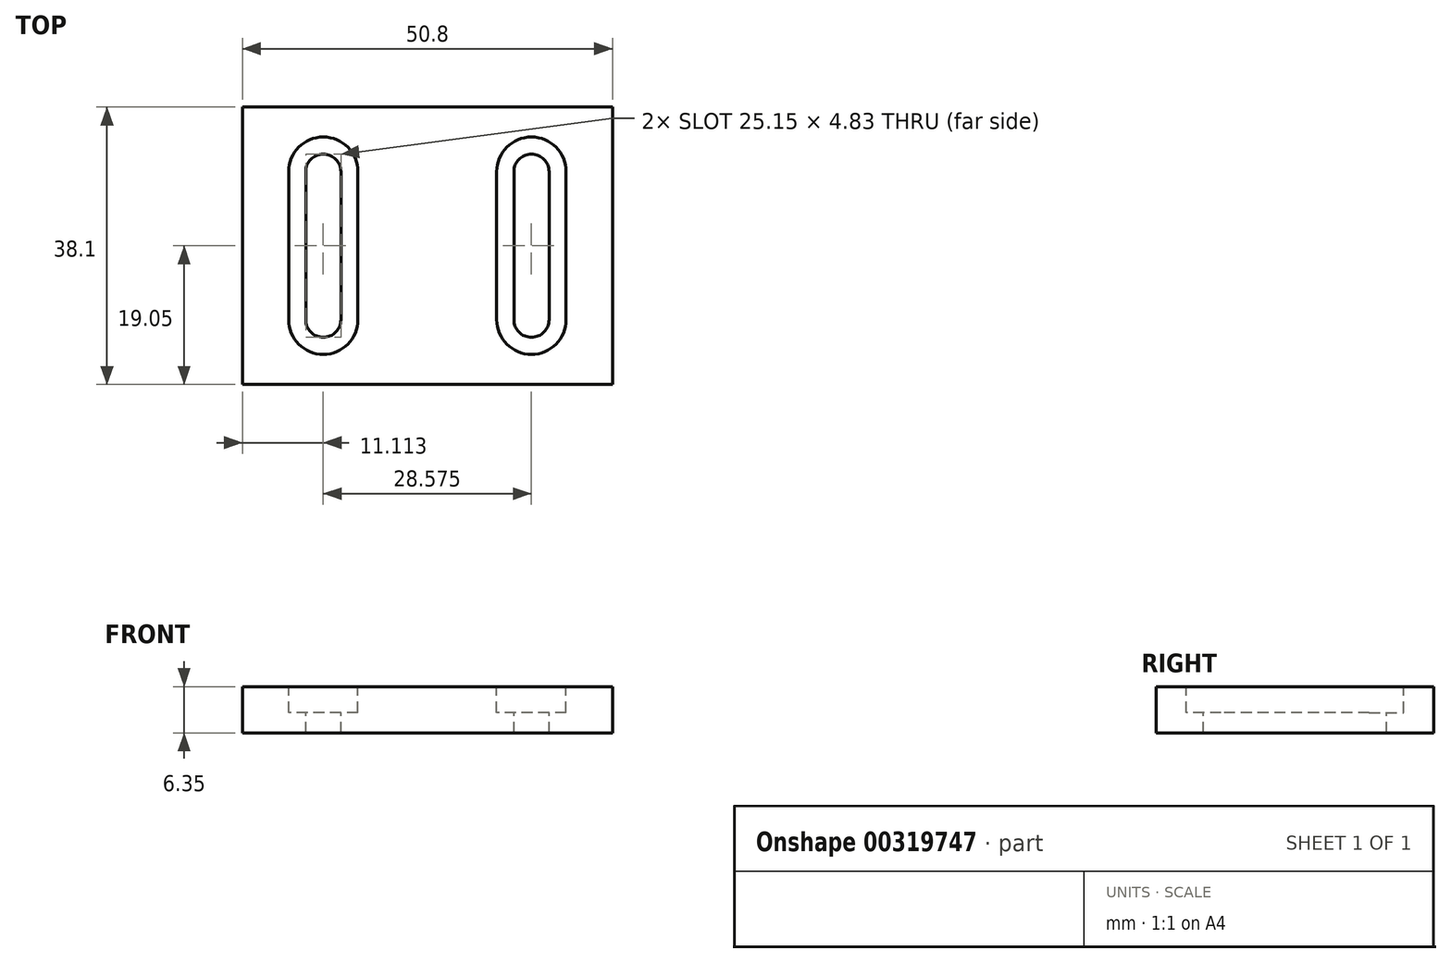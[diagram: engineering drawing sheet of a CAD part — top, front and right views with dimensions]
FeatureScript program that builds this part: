
annotation { "Feature Type Name" : "Feature", "Feature Type Description" : "" }
export const myFeature = defineFeature(function(context is Context, id is Id, definition is map)
    precondition{}
    {
        {
            var Q0;
            Q0=qCreatedBy(makeId("Top.planeOp"),FACE);
            var sketch = newSketch(context, id + "F0", { "sketchPlane" : qUnion([Q0])});
            skLineSegment(sketch, "E0.bottom", {"start": v(0, 0) * mm, "end": v(50.8, 0) * mm});
            skLineSegment(sketch, "E0.top", {"start": v(0, 38.1) * mm, "end": v(50.8, 38.1) * mm});
            skLineSegment(sketch, "E0.left", {"start": v(0, 0) * mm, "end": v(0, 38.1) * mm});
            skLineSegment(sketch, "E0.right", {"start": v(50.8, 0) * mm, "end": v(50.8, 38.1) * mm});
            skSolve(sketch);
        }
        {
            var Q0;
            Q0 = qSketchRegion(id + "F0", true);
            extrude(context, id + "F1", {"entities" : qUnion([Q0]), "depth" : 6.35 * mm});
        }
        {
            var Q0;
            Q0=makeQuery(id+"F1.opExtrude","CAP_FACE",FACE,{"disambiguationData":[OSD([sQuery(id+"F0.wireOp",EDGE,"E0.bottom"),sQuery(id+"F0.wireOp",EDGE,"E0.top"),sQuery(id+"F0.wireOp",EDGE,"E0.left"),sQuery(id+"F0.wireOp",EDGE,"E0.right")])],"isStart":false});
            var sketch = newSketch(context, id + "F2", { "sketchPlane" : qUnion([Q0])});
            skLineSegment(sketch, "E1.left", {"start": v(6.35, 29.2) * mm, "end": v(6.35, 8.9) * mm});
            skLineSegment(sketch, "E1.right", {"start": v(15.88, 29.21) * mm, "end": v(15.88, 8.9) * mm});
            skLineSegment(sketch, "E2.left", {"start": v(34.93, 29.21) * mm, "end": v(34.93, 8.9) * mm});
            skLineSegment(sketch, "E2.right", {"start": v(44.45, 29.21) * mm, "end": v(44.45, 8.9) * mm});
            skLineSegment(sketch, "E3", {"start": v(11.11, 33.97) * mm, "end": v(11.11, 33.97) * mm});
            skLineSegment(sketch, "E4", {"start": v(39.69, 33.97) * mm, "end": v(39.69, 33.97) * mm});
            skLineSegment(sketch, "E5", {"start": v(11.11, 4.13) * mm, "end": v(11.11, 4.13) * mm});
            skLineSegment(sketch, "E6", {"start": v(39.69, 4.13) * mm, "end": v(39.69, 4.13) * mm});
            skArc(sketch, "E7.filletArc", {"start": v(11.11, 33.97) * mm, "mid": v(7.74, 32.58) * mm, "end": v(6.35, 29.2) * mm});
            skPoint(sketch, "E8.newPointA", {"position": v(15.87, 33.97) * mm});
            skArc(sketch, "E8.filletArc", {"start": v(15.87, 29.21) * mm, "mid": v(14.48, 32.58) * mm, "end": v(11.11, 33.97) * mm});
            skArc(sketch, "E9.filletArc", {"start": v(11.11, 4.13) * mm, "mid": v(14.48, 5.52) * mm, "end": v(15.88, 8.9) * mm});
            skArc(sketch, "E10.filletArc", {"start": v(6.35, 8.9) * mm, "mid": v(7.74, 5.52) * mm, "end": v(11.11, 4.13) * mm});
            skPoint(sketch, "E11.newPointB", {"position": v(31.75, 33.97) * mm});
            skArc(sketch, "E11.filletArc", {"start": v(39.69, 33.97) * mm, "mid": v(36.32, 32.58) * mm, "end": v(34.93, 29.21) * mm});
            skArc(sketch, "E12.filletArc", {"start": v(44.45, 29.21) * mm, "mid": v(43.06, 32.58) * mm, "end": v(39.69, 33.97) * mm});
            skPoint(sketch, "E13.newPointA", {"position": v(44.45, 0) * mm});
            skPoint(sketch, "E13.newPointB", {"position": v(44.45, 4.13) * mm});
            skArc(sketch, "E13.filletArc", {"start": v(39.69, 4.13) * mm, "mid": v(43.06, 5.52) * mm, "end": v(44.45, 8.9) * mm});
            skArc(sketch, "E14.filletArc", {"start": v(34.93, 8.9) * mm, "mid": v(36.32, 5.52) * mm, "end": v(39.69, 4.13) * mm});
            skSolve(sketch);
        }
        {
            var Q0;
            Q0 = qSketchRegion(id + "F2", true);
            extrude(context, id + "F3", {"entities" : qUnion([Q0]), "operationType" : NewBodyOperationType.REMOVE, "oppositeDirection" : true, "depth" : 3.56 * mm});
        }
        {
            var Q0;
            Q0=makeQuery(id+"F3.boolean.opBoolean","COPY",FACE,{"derivedFrom":makeQuery(id+"F3.opExtrude","CAP_FACE",FACE,{"disambiguationData":[OSD([sQuery(id+"F2.wireOp",EDGE,"E1.bottom"),sQuery(id+"F2.wireOp",EDGE,"E1.top"),sQuery(id+"F2.wireOp",EDGE,"E1.left"),sQuery(id+"F2.wireOp",EDGE,"E1.right")])],"isStart":false})});
            var sketch = newSketch(context, id + "F4", { "sketchPlane" : qUnion([Q0])});
            skLineSegment(sketch, "E15.left", {"start": v(8.7, 29.2) * mm, "end": v(8.7, 8.9) * mm});
            skLineSegment(sketch, "E15.right", {"start": v(13.53, 29.21) * mm, "end": v(13.53, 8.9) * mm});
            skLineSegment(sketch, "E16.bottom", {"start": v(39.69, 31.62) * mm, "end": v(39.69, 31.62) * mm});
            skLineSegment(sketch, "E16.top", {"start": v(39.69, 6.48) * mm, "end": v(39.69, 6.48) * mm});
            skLineSegment(sketch, "E16.left", {"start": v(37.27, 29.2) * mm, "end": v(37.27, 8.9) * mm});
            skLineSegment(sketch, "E16.right", {"start": v(42.1, 29.21) * mm, "end": v(42.1, 8.9) * mm});
            skPoint(sketch, "E17.visualSharp", {"position": v(37.27, 31.62) * mm});
            skArc(sketch, "E17.filletArc", {"start": v(39.69, 31.62) * mm, "mid": v(37.98, 30.92) * mm, "end": v(37.27, 29.2) * mm});
            skPoint(sketch, "E18.visualSharp", {"position": v(42.1, 31.62) * mm});
            skArc(sketch, "E18.filletArc", {"start": v(42.1, 29.21) * mm, "mid": v(41.4, 30.92) * mm, "end": v(39.69, 31.62) * mm});
            skPoint(sketch, "E19.visualSharp", {"position": v(42.1, 6.48) * mm});
            skArc(sketch, "E19.filletArc", {"start": v(39.69, 6.48) * mm, "mid": v(41.4, 7.18) * mm, "end": v(42.1, 8.9) * mm});
            skPoint(sketch, "E20.visualSharp", {"position": v(37.27, 6.48) * mm});
            skArc(sketch, "E20.filletArc", {"start": v(37.27, 8.9) * mm, "mid": v(37.98, 7.18) * mm, "end": v(39.69, 6.48) * mm});
            skArc(sketch, "E21", {"start": v(8.7, 29.2) * mm, "mid": v(11.11, 31.62) * mm, "end": v(13.53, 29.21) * mm});
            skArc(sketch, "E22", {"start": v(13.53, 8.9) * mm, "mid": v(11.11, 6.48) * mm, "end": v(8.7, 8.9) * mm});
            skSolve(sketch);
        }
        {
            var Q0;
            Q0 = qSketchRegion(id + "F4", true);
            extrude(context, id + "F5", {"entities" : qUnion([Q0]), "operationType" : NewBodyOperationType.REMOVE, "oppositeDirection" : true, "depth" : 25.4 * mm});
        }
    });
